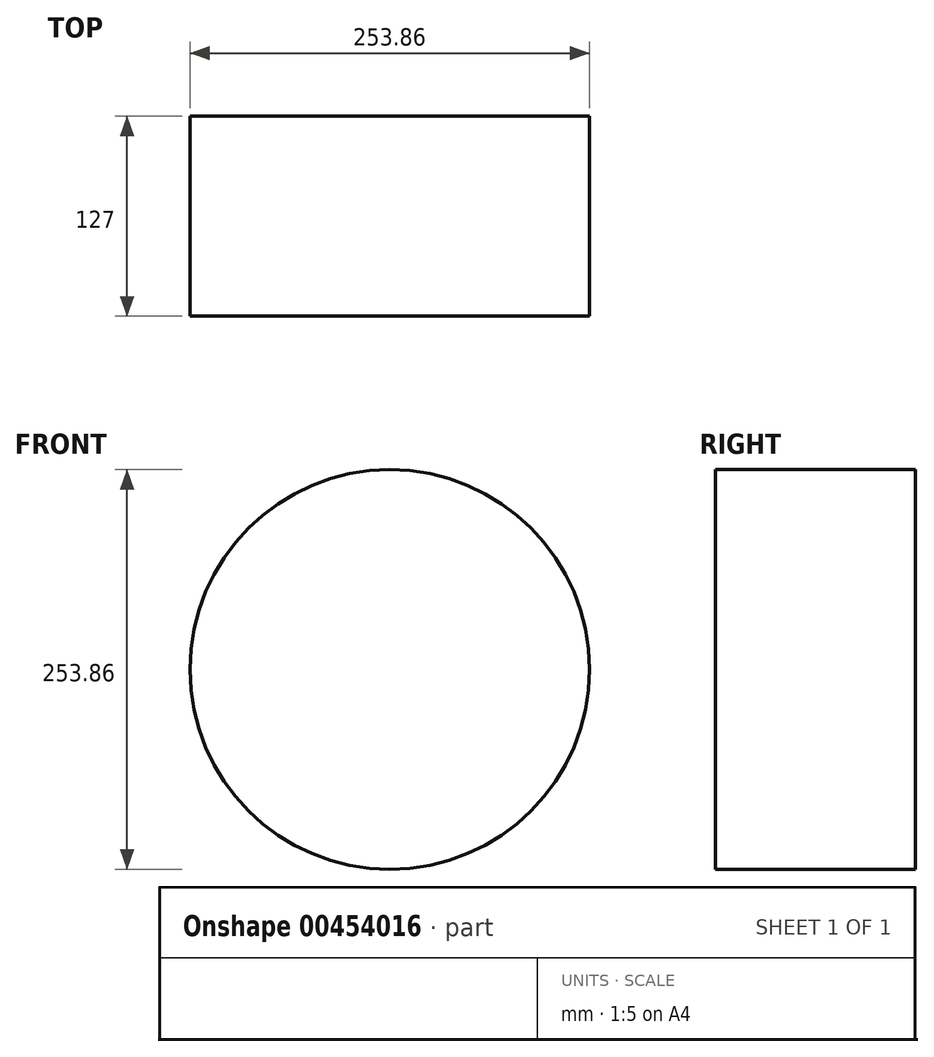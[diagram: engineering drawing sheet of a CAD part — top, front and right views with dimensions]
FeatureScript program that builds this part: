
annotation { "Feature Type Name" : "Feature", "Feature Type Description" : "" }
export const myFeature = defineFeature(function(context is Context, id is Id, definition is map)
    precondition{}
    {
        {
            var Q0;
            Q0=qCreatedBy(makeId("Front.planeOp"),FACE);
            var sketch = newSketch(context, id + "F0", { "sketchPlane" : qUnion([Q0])});
            skCircle(sketch, "E0", {"center": v(0, 0) * mm, "radius": 126.93 * mm});
            skSolve(sketch);
        }
        {
            var Q0;
            Q0=sQuery(id+"F0.wireOp",EDGE,"E0");
            extrude(context, id + "F1", {"bodyType" : ToolBodyType.SURFACE, "surfaceEntities" : qUnion([Q0]), "depth" : 127 * mm});
        }
    });
